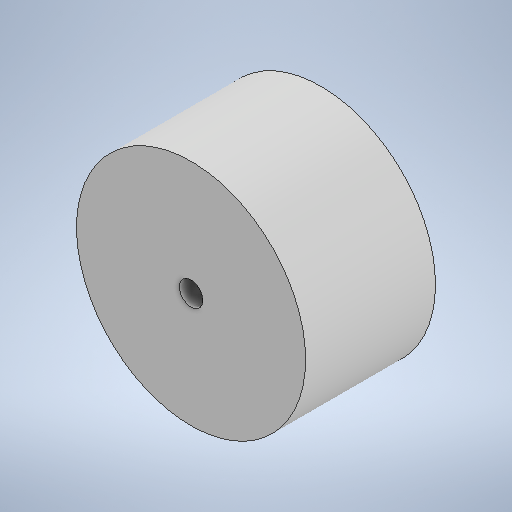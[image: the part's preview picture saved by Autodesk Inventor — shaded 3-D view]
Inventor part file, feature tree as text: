
AUTODESK INVENTOR PART (.ipt)
format: ipt  version: 2025.3 (Build 293356000, 356)  size: 198,144 bytes
history: native  units: mm
features: other x1, extrude x1, sketch x1
ambient origin geometry x8: Origin, YZ Plane, XZ Plane, XY Plane, X Axis, Y Axis, Z Axis, Center Point
bodies: Body1 (feature_tree)
feature tree (3):
  other  "솔리드1"
  extrude  "돌출1"  Depth=97.0mm
  sketch  "스케치1"
